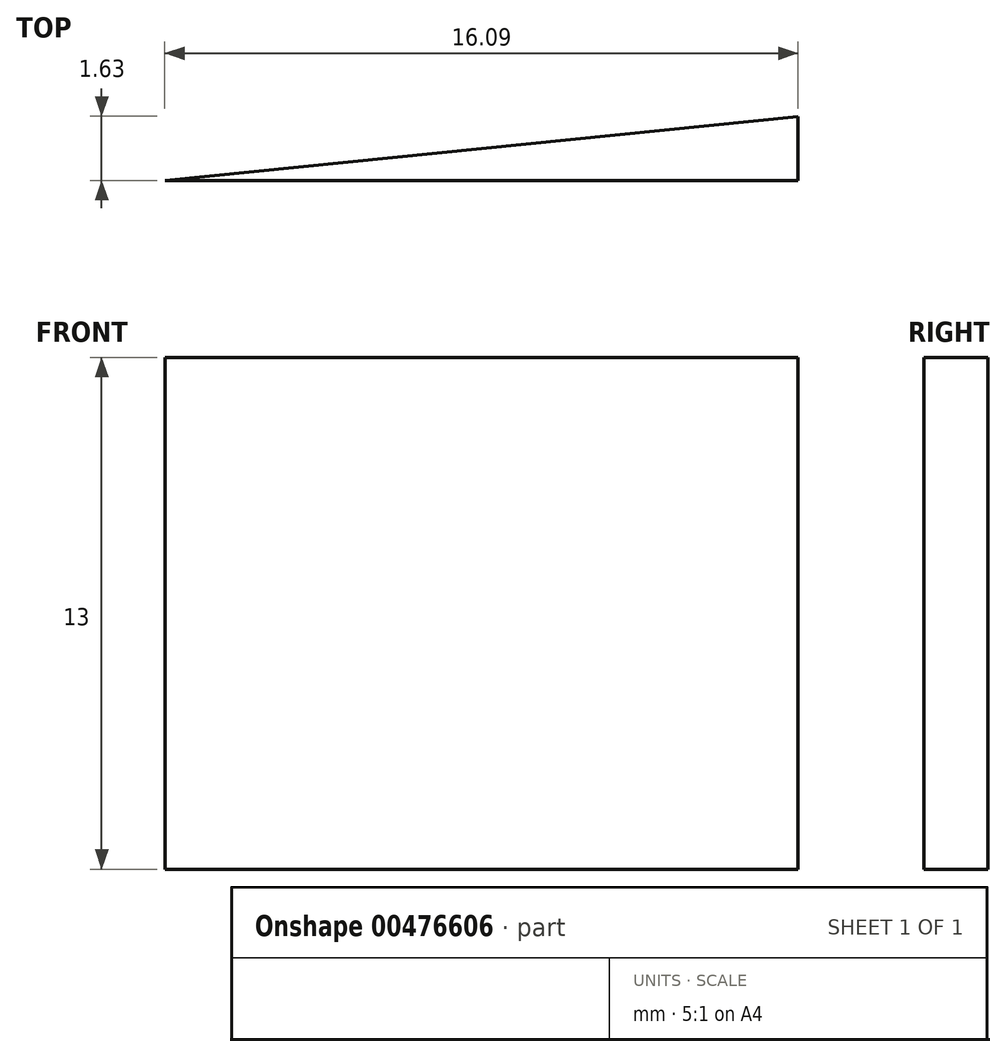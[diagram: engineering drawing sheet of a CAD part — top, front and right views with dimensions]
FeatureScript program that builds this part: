
annotation { "Feature Type Name" : "Feature", "Feature Type Description" : "" }
export const myFeature = defineFeature(function(context is Context, id is Id, definition is map)
    precondition{}
    {
        {
            var Q0;
            Q0=qCreatedBy(makeId("Top.planeOp"),FACE);
            var sketch = newSketch(context, id + "F0", { "sketchPlane" : qUnion([Q0])});
            skLineSegment(sketch, "E0", {"start": v(-1.5, 0) * mm, "end": v(-17.58, 0) * mm});
            skLineSegment(sketch, "E1", {"start": v(-1.5, 1.63) * mm, "end": v(-1.5, 0) * mm});
            skPoint(sketch, "E2.end.orphan", {"position": v(-10.5, 0) * mm});
            skLineSegment(sketch, "E3", {"start": v(-17.58, 0) * mm, "end": v(-1.5, 1.63) * mm});
            skSolve(sketch);
        }
        {
            var Q0;
            Q0 = qSketchRegion(id + "F0", true);
            extrude(context, id + "F1", {"entities" : qUnion([Q0]), "depth" : 13 * mm});
        }
    });
